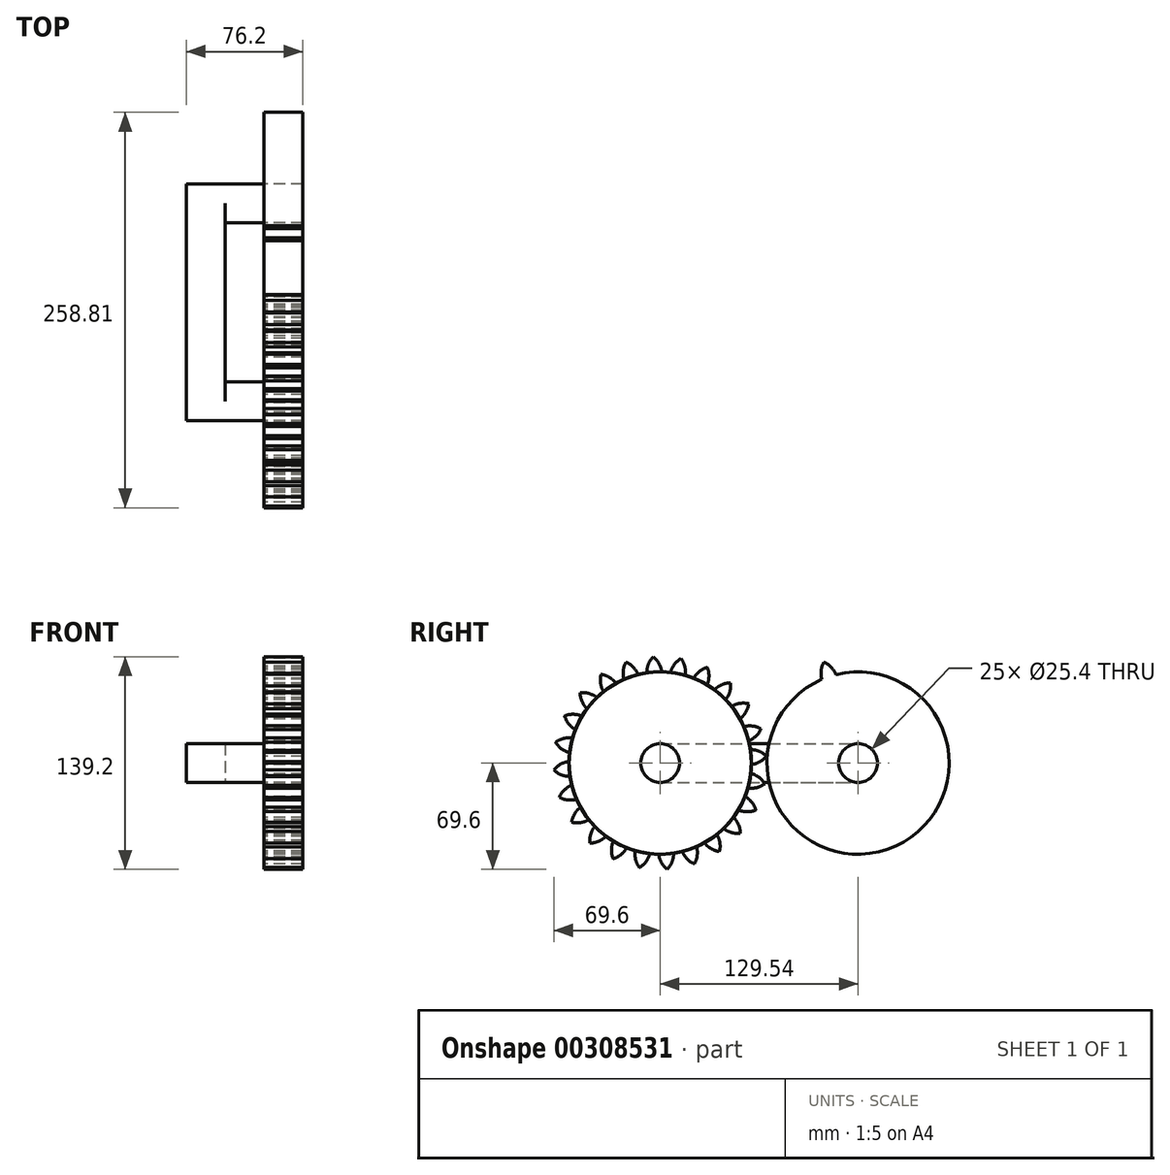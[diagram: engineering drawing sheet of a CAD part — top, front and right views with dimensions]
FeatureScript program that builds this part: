
annotation { "Feature Type Name" : "Feature", "Feature Type Description" : "" }
export const myFeature = defineFeature(function(context is Context, id is Id, definition is map)
    precondition{}
    {
        {
            var Q0;
            Q0=qCreatedBy(makeId("Right.planeOp"),FACE);
            var sketch = newSketch(context, id + "F0", { "sketchPlane" : qUnion([Q0])});
            skLineSegment(sketch, "E0.bottom", {"start": v(0, 0) * mm, "end": v(129.54, 0) * mm});
            skLineSegment(sketch, "E0.top", {"start": v(0, 25.4) * mm, "end": v(129.54, 25.4) * mm});
            skLineSegment(sketch, "E0.left", {"start": v(0, 0) * mm, "end": v(0, 25.4) * mm});
            skLineSegment(sketch, "E0.right", {"start": v(129.54, 0) * mm, "end": v(129.54, 25.4) * mm});
            skCircle(sketch, "E1", {"center": v(0, 12.7) * mm, "radius": 12.7 * mm});
            skCircle(sketch, "E2", {"center": v(129.54, 12.7) * mm, "radius": 12.7 * mm});
            skSolve(sketch);
        }
        {
            var Q0;
            Q0 = qSketchRegion(id + "F0", true);
            extrude(context, id + "F1", {"entities" : qUnion([Q0]), "depth" : 25.4 * mm});
        }
        {
            var Q0;
            {var subQ0=sQuery(id+"F0.wireOp",EDGE,"E0.left");Q0=makeQuery(id+"F0.imprint","IMPRINT",FACE,{"disambiguationData":[TD([[makeQuery(id+"F0.imprint","IMPRINT",EDGE,{"derivedFrom":subQ0}),1.0]])]});}
            var Q1;
            {var subQ0=sQuery(id+"F0.wireOp",EDGE,"E0.left");Q1=makeQuery(id+"F0.imprint","IMPRINT",FACE,{"disambiguationData":[TD([[makeQuery(id+"F0.imprint","IMPRINT",EDGE,{"derivedFrom":subQ0}),-1.0]])]});}
            var Q2;
            {var subQ0=sQuery(id+"F0.wireOp",EDGE,"E0.right");Q2=makeQuery(id+"F0.imprint","IMPRINT",FACE,{"disambiguationData":[TD([[makeQuery(id+"F0.imprint","IMPRINT",EDGE,{"derivedFrom":subQ0}),1.0]])]});}
            var Q3;
            {var subQ0=sQuery(id+"F0.wireOp",EDGE,"E0.right");Q3=makeQuery(id+"F0.imprint","IMPRINT",FACE,{"disambiguationData":[TD([[makeQuery(id+"F0.imprint","IMPRINT",EDGE,{"derivedFrom":subQ0}),-1.0]])]});}
            extrude(context, id + "F2", {"entities" : qUnion([Q0, Q1, Q2, Q3]), "operationType" : NewBodyOperationType.ADD, "depth" : 50.8 * mm});
        }
        {
            var Q0;
            Q0=makeQuery(id+"F2.opExtrude","CAP_FACE",FACE,{"disambiguationData":[OSD([sQuery(id+"F0.wireOp",EDGE,"E1")])],"isStart":false});
            var sketch = newSketch(context, id + "F3", { "sketchPlane" : qUnion([Q0])});
            skCircle(sketch, "E3", {"center": v(0, 12.7) * mm, "radius": 12.7 * mm});
            skCircle(sketch, "E4", {"center": v(0, 12.7) * mm, "radius": 53.72 * mm, "construction": true});
            skCircle(sketch, "E5", {"center": v(0, 12.7) * mm, "radius": 58.67 * mm, "construction": true});
            skCircle(sketch, "E6", {"center": v(0, 12.7) * mm, "radius": 63.5 * mm, "construction": true});
            skLineSegment(sketch, "E7", {"start": v(0, 12.7) * mm, "end": v(0, 98.3) * mm, "construction": true});
            skLineSegment(sketch, "E8", {"start": v(0, 12.7) * mm, "end": v(-7.31, 124.3) * mm, "construction": true});
            skLineSegment(sketch, "E9", {"start": v(0, 76.2) * mm, "end": v(-54.07, 76.2) * mm, "construction": true});
            skLineSegment(sketch, "E10", {"start": v(0, 76.2) * mm, "end": v(-50.1, 57.96) * mm, "construction": true});
            skCircle(sketch, "E11", {"center": v(0, 12.7) * mm, "radius": 59.67 * mm});
            skCircle(sketch, "E12", {"center": v(0, 76.2) * mm, "radius": 14.6 * mm, "construction": true});
            skCircle(sketch, "E13", {"center": v(-13.57, 70.8) * mm, "radius": 14.6 * mm, "construction": true});
            skArc(sketch, "E14", {"start": v(0, 76.2) * mm, "mid": v(-1.87, 79.56) * mm, "end": v(-4.56, 82.3) * mm});
            skArc(sketch, "E15", {"start": v(0.95, 72.36) * mm, "mid": v(0.65, 74.33) * mm, "end": v(0, 76.2) * mm});
            skArc(sketch, "E16.MirrorCS", {"start": v(-8.29, 75.66) * mm, "mid": v(-6.87, 79.23) * mm, "end": v(-4.56, 82.3) * mm});
            skArc(sketch, "E17.MirrorCS", {"start": v(-8.73, 71.73) * mm, "mid": v(-8.69, 73.71) * mm, "end": v(-8.29, 75.66) * mm});
            skSolve(sketch);
        }
        {
            var Q0;
            Q0 = qSketchRegion(id + "F3", true);
            extrude(context, id + "F4", {"entities" : qUnion([Q0]), "depth" : 25.4 * mm});
        }
        {
            var Q0;
            Q0=makeQuery(id+"F4.opExtrude","SWEPT_BODY",BODY,{"disambiguationData":[OSD([sQuery(id+"F3.wireOp",EDGE,"E3"),sQuery(id+"F3.wireOp",EDGE,"E11"),sQuery(id+"F3.wireOp",EDGE,"E14"),sQuery(id+"F3.wireOp",EDGE,"E15"),sQuery(id+"F3.wireOp",EDGE,"E16.MirrorCS"),sQuery(id+"F3.wireOp",EDGE,"E17.MirrorCS")])]});
            var Q1;
            Q1=makeQuery(id+"F4.opExtrude","SWEPT_FACE",FACE,{"disambiguationData":[OSD([sQuery(id+"F3.wireOp",EDGE,"E11")])]});
            circularPattern(context, id + "F5", {"entities" : qUnion([Q0]), "axis" : qUnion([Q1]), "angle" : 15 * degree, "instanceCount" : 24});
        }
        {
            var Q0;
            Q0=makeQuery(id+"F2.opExtrude","CAP_FACE",FACE,{"disambiguationData":[OSD([sQuery(id+"F0.wireOp",EDGE,"E1")])],"isStart":false});
            extrude(context, id + "F6", {"entities" : qUnion([Q0]), "depth" : 25.4 * mm});
        }
        {
            var Q0;
            Q0=makeQuery(id+"F5.opPattern","COPY",BODY,{"derivedFrom":makeQuery(id+"F4.opExtrude","SWEPT_BODY",BODY,{"disambiguationData":[OSD([sQuery(id+"F3.wireOp",EDGE,"E3"),sQuery(id+"F3.wireOp",EDGE,"E11"),sQuery(id+"F3.wireOp",EDGE,"E14"),sQuery(id+"F3.wireOp",EDGE,"E15"),sQuery(id+"F3.wireOp",EDGE,"E16.MirrorCS"),sQuery(id+"F3.wireOp",EDGE,"E17.MirrorCS")])]}),"instanceName":"23"});
            transform(context, id + "F7", {"entities" : qUnion([Q0]), "transformType" : TransformType.TRANSLATION_3D, "dx" : 0 * mm, "dy" : 129.54 * mm, "dz" : 0 * mm, "makeCopy" : true});
        }
        {
            var Q0;
            Q0=makeQuery(id+"F2.opExtrude","CAP_FACE",FACE,{"disambiguationData":[OSD([sQuery(id+"F0.wireOp",EDGE,"E2")])],"isStart":false});
            extrude(context, id + "F8", {"entities" : qUnion([Q0]), "depth" : 25.4 * mm});
        }
    });
